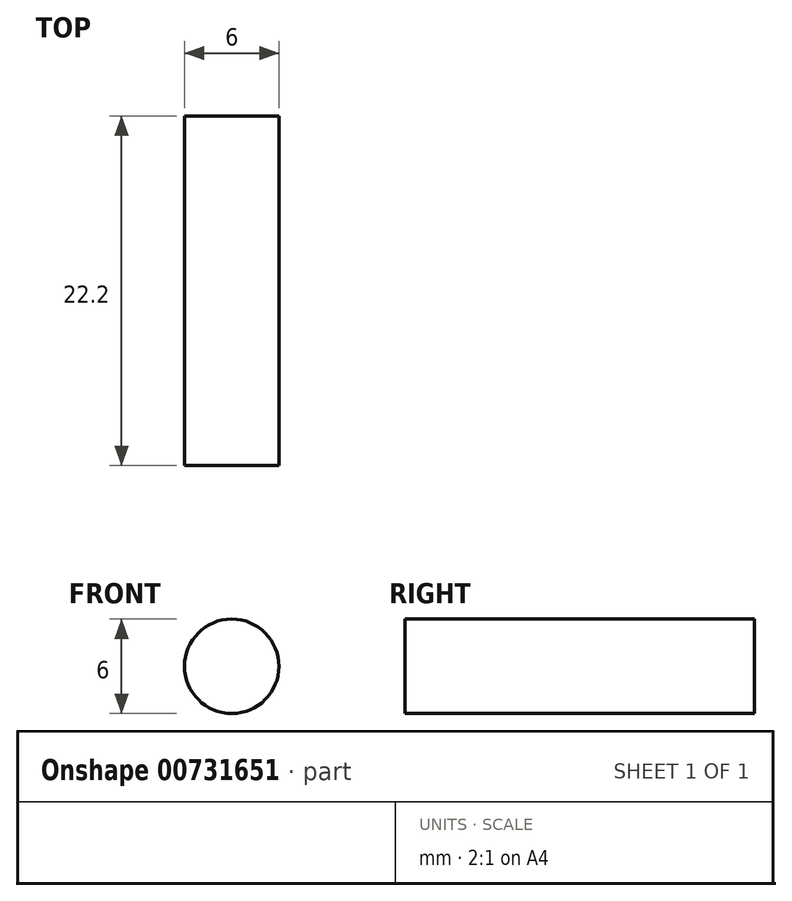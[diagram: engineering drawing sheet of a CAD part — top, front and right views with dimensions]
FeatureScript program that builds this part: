
annotation { "Feature Type Name" : "Feature", "Feature Type Description" : "" }
export const myFeature = defineFeature(function(context is Context, id is Id, definition is map)
    precondition{}
    {
        {
            var Q0;
            Q0=qCreatedBy(makeId("Front.planeOp"),FACE);
            var sketch = newSketch(context, id + "F0", { "sketchPlane" : qUnion([Q0])});
            skCircle(sketch, "E0", {"center": v(0, 0) * mm, "radius": 3 * mm});
            skSolve(sketch);
        }
        {
            var Q0;
            Q0 = qSketchRegion(id + "F0", true);
            extrude(context, id + "F1", {"entities" : qUnion([Q0]), "depth" : 22.2 * mm, "offsetDistance" : 25 * mm});
        }
    });
